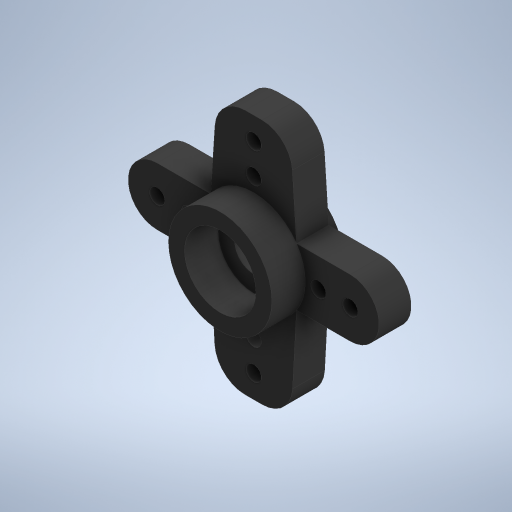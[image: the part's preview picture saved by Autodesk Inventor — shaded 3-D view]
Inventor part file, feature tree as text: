
AUTODESK INVENTOR PART (.ipt)
format: ipt  version: 2023 (Build 270158000, 158)  size: 467,456 bytes
history: native  units: mm
features: sketch x10, extrude x10, other x1, fillet x1
ambient origin geometry x8: Origin, YZ Plane, XZ Plane, XY Plane, X Axis, Y Axis, Z Axis, Center Point
bodies: Body1 (feature_tree)
feature tree (22):
  other  "솔리드1"
  sketch  "스케치1"
  extrude  "돌출1"  Depth=5.0mm
  extrude  "돌출2"  Depth=1.9mm
  extrude  "돌출3"  Depth=16.5mm
  extrude  "돌출4"  Depth=29.0mm
  extrude  "돌출5"  Depth=1.0mm
  sketch  "스케치4"
  extrude  "돌출6"  Depth=1.0mm
  extrude  "돌출7"  Depth=1.0mm
  extrude  "돌출8"  Depth=1.0mm
  extrude  "돌출9"  Depth=10.0mm
  extrude  "돌출10"  Depth=10.0mm
  fillet  "모깎기1"  Radius=16.6mm
  sketch  "스케치11"
  sketch  "스케치2"
  sketch  "스케치3"
  sketch  "스케치5"
  sketch  "스케치6"
  sketch  "스케치7"
  sketch  "스케치9"
  sketch  "스케치10"
